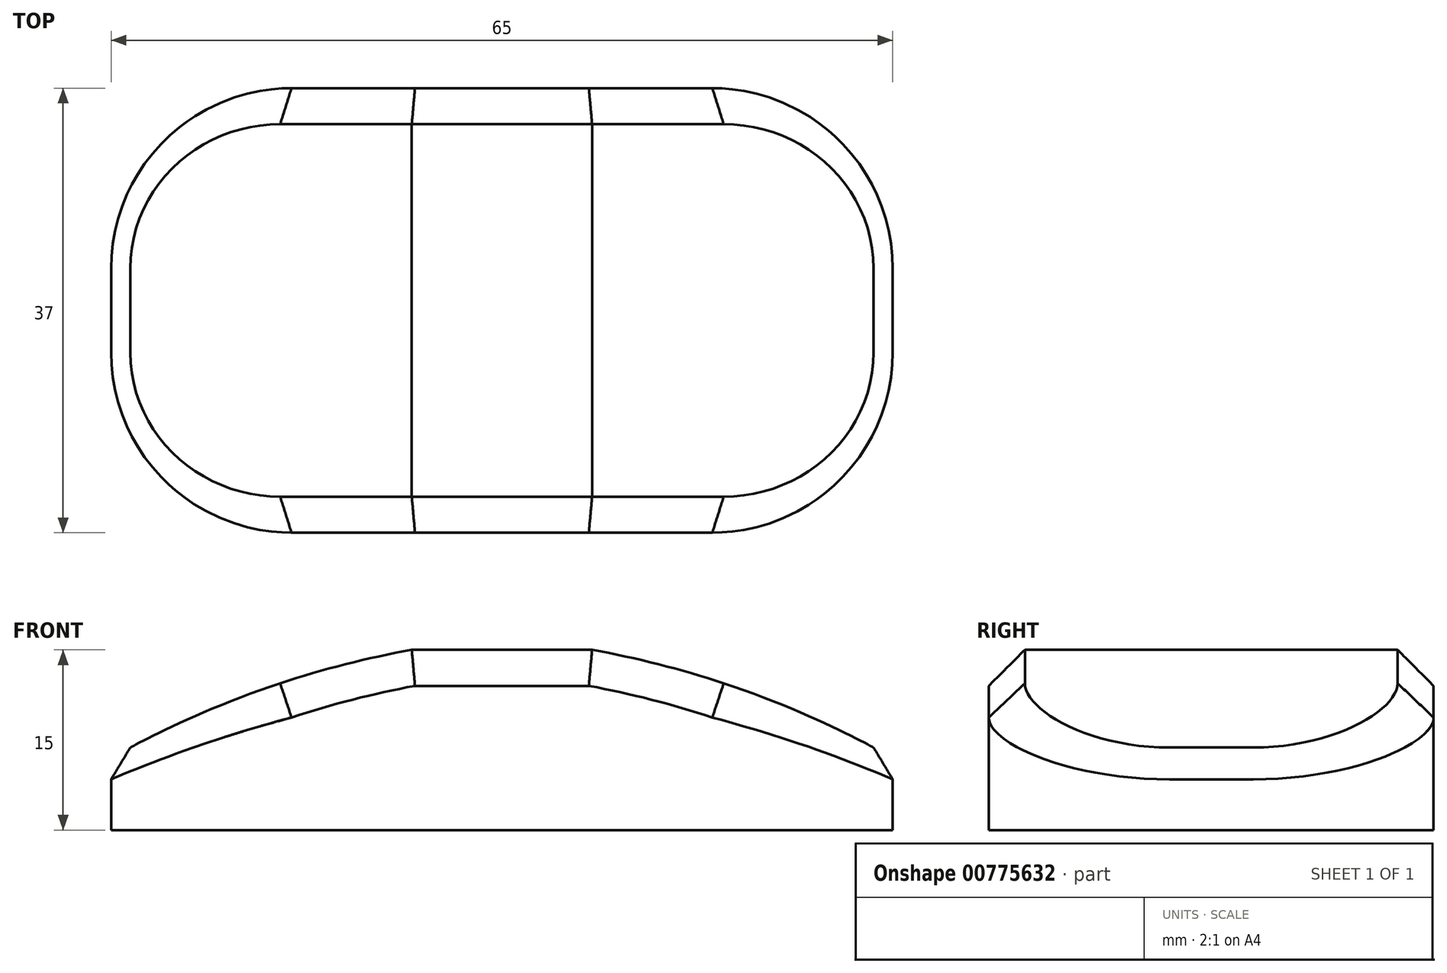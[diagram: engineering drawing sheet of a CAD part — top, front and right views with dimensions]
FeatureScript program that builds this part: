
annotation { "Feature Type Name" : "Feature", "Feature Type Description" : "" }
export const myFeature = defineFeature(function(context is Context, id is Id, definition is map)
    precondition{}
    {
        {
            var Q0;
            Q0=qCreatedBy(makeId("Top.planeOp"),FACE);
            var sketch = newSketch(context, id + "F0", { "sketchPlane" : qUnion([Q0])});
            skLineSegment(sketch, "E0.bottom", {"start": v(32.5, -18.5) * mm, "end": v(-32.5, -18.5) * mm});
            skLineSegment(sketch, "E0.top", {"start": v(32.5, 18.5) * mm, "end": v(-32.5, 18.5) * mm});
            skLineSegment(sketch, "E0.left", {"start": v(32.5, -18.5) * mm, "end": v(32.5, 18.5) * mm});
            skLineSegment(sketch, "E0.right", {"start": v(-32.5, -18.5) * mm, "end": v(-32.5, 18.5) * mm});
            skPoint(sketch, "E0.middle", {"position": v(0, 0) * mm});
            skSolve(sketch);
        }
        {
            var Q0;
            Q0=makeQuery(id+"F0.imprint","IMPRINT",FACE,{"disambiguationData":[TD([[makeQuery(id+"F0.imprint","IMPRINT",EDGE,{"derivedFrom":sQuery(id+"F0.wireOp",EDGE,"E0.bottom")}),-1.0]])]});
            extrude(context, id + "F1", {"entities" : qUnion([Q0]), "depth" : 15 * mm, "offsetDistance" : 25 * mm});
        }
        {
            var Q0;
            Q0=makeQuery(id+"F1.opExtrude","SWEPT_FACE",FACE,{"disambiguationData":[OSD([sQuery(id+"F0.wireOp",EDGE,"E0.bottom")])]});
            var sketch = newSketch(context, id + "F2", { "sketchPlane" : qUnion([Q0])});
            skLineSegment(sketch, "E1.bottom", {"start": v(-32.5, 15) * mm, "end": v(32.5, 15) * mm});
            skLineSegment(sketch, "E1.left", {"start": v(-32.5, 15) * mm, "end": v(-32.5, 6) * mm});
            skLineSegment(sketch, "E1.right", {"start": v(32.5, 15) * mm, "end": v(32.5, 0) * mm});
            skArc(sketch, "E2", {"start": v(-7.5, 15) * mm, "mid": v(-20.38, 11.55) * mm, "end": v(-32.5, 6) * mm});
            skArc(sketch, "E3", {"start": v(32.5, 6) * mm, "mid": v(20.38, 11.55) * mm, "end": v(7.5, 15) * mm});
            skSolve(sketch);
        }
        {
            var Q0;
            {var subQ0=sQuery(id+"F2.wireOp",EDGE,"E1.left");Q0=makeQuery(id+"F2.imprint","IMPRINT",FACE,{"disambiguationData":[TD([[makeQuery(id+"F2.imprint","IMPRINT",EDGE,{"derivedFrom":subQ0}),1.0]])]});}
            var Q1;
            {var subQ3=sQuery(id+"F2.wireOp",EDGE,"E3");Q1=makeQuery(id+"F2.imprint","IMPRINT",FACE,{"disambiguationData":[TD([[makeQuery(id+"F2.imprint","IMPRINT",EDGE,{"derivedFrom":subQ3}),-1.0]])]});}
            extrude(context, id + "F3", {"entities" : qUnion([Q0, Q1]), "operationType" : NewBodyOperationType.REMOVE, "endBound" : BoundingType.THROUGH_ALL, "oppositeDirection" : true, "depth" : 25 * mm, "offsetDistance" : 25 * mm});
        }
        {
            var Q0;
            Q0=makeQuery(id+"F1.opExtrude","SWEPT_EDGE",EDGE,{"disambiguationData":[OSD([sQuery(id+"F0.wireOp",EDGE,"E0.bottom"),sQuery(id+"F0.wireOp",EDGE,"E0.right")])]});
            var Q1;
            Q1=makeQuery(id+"F1.opExtrude","SWEPT_EDGE",EDGE,{"disambiguationData":[OSD([sQuery(id+"F0.wireOp",EDGE,"E0.bottom"),sQuery(id+"F0.wireOp",EDGE,"E0.left")])]});
            var Q2;
            Q2=makeQuery(id+"F1.opExtrude","SWEPT_EDGE",EDGE,{"disambiguationData":[OSD([sQuery(id+"F0.wireOp",EDGE,"E0.top"),sQuery(id+"F0.wireOp",EDGE,"E0.left")])]});
            var Q3;
            Q3=makeQuery(id+"F1.opExtrude","SWEPT_EDGE",EDGE,{"disambiguationData":[OSD([sQuery(id+"F0.wireOp",EDGE,"E0.top"),sQuery(id+"F0.wireOp",EDGE,"E0.right")])]});
            fillet(context, id + "F4", {"entities" : qUnion([Q0, Q1, Q2, Q3]), "radius" : 15 * mm, "tangentPropagation" : true, "allowEdgeOverflow" : false});
        }
        {
            var Q0;
            Q0=makeQuery(id+"F3.boolean.opBoolean","INTERSECT",EDGE,{"derivedFrom":[makeQuery(id+"F1.opExtrude","SWEPT_FACE",FACE,{"disambiguationData":[OSD([sQuery(id+"F0.wireOp",EDGE,"E0.top")])]}),makeQuery(id+"F3.opExtrude","SWEPT_FACE",FACE,{"disambiguationData":[OSD([sQuery(id+"F2.wireOp",EDGE,"E2")])]})]});
            var Q1;
            Q1=makeQuery(id+"F4.opFillet","BLEND_EDGE",EDGE,{"blendedFrom":[makeQuery(id+"F1.opExtrude","SWEPT_EDGE",EDGE,{"disambiguationData":[OSD([sQuery(id+"F0.wireOp",EDGE,"E0.top"),sQuery(id+"F0.wireOp",EDGE,"E0.right")])]}),makeQuery(id+"F3.boolean.opBoolean","COPY",FACE,{"derivedFrom":makeQuery(id+"F3.opExtrude","SWEPT_FACE",FACE,{"disambiguationData":[OSD([sQuery(id+"F2.wireOp",EDGE,"E2")])]})})],"blendedInto":[makeQuery(id+"F3.boolean.opBoolean","COPY",FACE,{"derivedFrom":makeQuery(id+"F3.opExtrude","SWEPT_FACE",FACE,{"disambiguationData":[OSD([sQuery(id+"F2.wireOp",EDGE,"E2")])]})})]});
            var Q2;
            Q2=makeQuery(id+"F4.opFillet","BLEND_EDGE",EDGE,{"blendedFrom":[makeQuery(id+"F1.opExtrude","SWEPT_EDGE",EDGE,{"disambiguationData":[OSD([sQuery(id+"F0.wireOp",EDGE,"E0.bottom"),sQuery(id+"F0.wireOp",EDGE,"E0.right")])]}),makeQuery(id+"F3.boolean.opBoolean","COPY",FACE,{"derivedFrom":makeQuery(id+"F3.opExtrude","SWEPT_FACE",FACE,{"disambiguationData":[OSD([sQuery(id+"F2.wireOp",EDGE,"E2")])]})})],"blendedInto":[makeQuery(id+"F3.boolean.opBoolean","COPY",FACE,{"derivedFrom":makeQuery(id+"F3.opExtrude","SWEPT_FACE",FACE,{"disambiguationData":[OSD([sQuery(id+"F2.wireOp",EDGE,"E2")])]})})]});
            var Q3;
            Q3=makeQuery(id+"F3.boolean.opBoolean","COPY",EDGE,{"derivedFrom":makeQuery(id+"F3.opExtrude","CAP_EDGE",EDGE,{"disambiguationData":[OSD([sQuery(id+"F2.wireOp",EDGE,"E2")])],"isStart":true})});
            var Q4;
            Q4=makeQuery(id+"F3.boolean.opBoolean","COPY",EDGE,{"derivedFrom":makeQuery(id+"F3.opExtrude","CAP_EDGE",EDGE,{"disambiguationData":[OSD([sQuery(id+"F2.wireOp",EDGE,"E3")])],"isStart":true})});
            var Q5;
            Q5=makeQuery(id+"F4.opFillet","BLEND_EDGE",EDGE,{"blendedFrom":[makeQuery(id+"F1.opExtrude","SWEPT_EDGE",EDGE,{"disambiguationData":[OSD([sQuery(id+"F0.wireOp",EDGE,"E0.bottom"),sQuery(id+"F0.wireOp",EDGE,"E0.left")])]}),makeQuery(id+"F3.boolean.opBoolean","COPY",FACE,{"derivedFrom":makeQuery(id+"F3.opExtrude","SWEPT_FACE",FACE,{"disambiguationData":[OSD([sQuery(id+"F2.wireOp",EDGE,"E3")])]})})],"blendedInto":[makeQuery(id+"F3.boolean.opBoolean","COPY",FACE,{"derivedFrom":makeQuery(id+"F3.opExtrude","SWEPT_FACE",FACE,{"disambiguationData":[OSD([sQuery(id+"F2.wireOp",EDGE,"E3")])]})})]});
            var Q6;
            Q6=makeQuery(id+"F4.opFillet","BLEND_EDGE",EDGE,{"blendedFrom":[makeQuery(id+"F1.opExtrude","SWEPT_EDGE",EDGE,{"disambiguationData":[OSD([sQuery(id+"F0.wireOp",EDGE,"E0.top"),sQuery(id+"F0.wireOp",EDGE,"E0.left")])]}),makeQuery(id+"F3.boolean.opBoolean","COPY",FACE,{"derivedFrom":makeQuery(id+"F3.opExtrude","SWEPT_FACE",FACE,{"disambiguationData":[OSD([sQuery(id+"F2.wireOp",EDGE,"E3")])]})})],"blendedInto":[makeQuery(id+"F3.boolean.opBoolean","COPY",FACE,{"derivedFrom":makeQuery(id+"F3.opExtrude","SWEPT_FACE",FACE,{"disambiguationData":[OSD([sQuery(id+"F2.wireOp",EDGE,"E3")])]})})]});
            var Q7;
            Q7=makeQuery(id+"F3.boolean.opBoolean","INTERSECT",EDGE,{"derivedFrom":[makeQuery(id+"F1.opExtrude","SWEPT_FACE",FACE,{"disambiguationData":[OSD([sQuery(id+"F0.wireOp",EDGE,"E0.top")])]}),makeQuery(id+"F3.opExtrude","SWEPT_FACE",FACE,{"disambiguationData":[OSD([sQuery(id+"F2.wireOp",EDGE,"E3")])]})]});
            var Q8;
            Q8=makeQuery(id+"F1.opExtrude","CAP_EDGE",EDGE,{"disambiguationData":[OSD([sQuery(id+"F0.wireOp",EDGE,"E0.bottom")])],"isStart":false});
            var Q9;
            Q9=makeQuery(id+"F3.boolean.opBoolean","COPY",EDGE,{"derivedFrom":makeQuery(id+"F3.opExtrude","SWEPT_EDGE",EDGE,{"disambiguationData":[OSD([sQuery(id+"F0.wireOp",EDGE,"E0.bottom"),sQuery(id+"F0.wireOp",EDGE,"E0.right"),sQuery(id+"F2.wireOp",EDGE,"E1.left"),sQuery(id+"F2.wireOp",EDGE,"E2")])]})});
            var Q10;
            Q10=makeQuery(id+"F3.boolean.opBoolean","COPY",EDGE,{"derivedFrom":makeQuery(id+"F3.opExtrude","SWEPT_EDGE",EDGE,{"disambiguationData":[OSD([sQuery(id+"F2.wireOp",EDGE,"E1.right"),sQuery(id+"F2.wireOp",EDGE,"E3")])]})});
            var Q11;
            Q11=makeQuery(id+"F1.opExtrude","CAP_EDGE",EDGE,{"disambiguationData":[OSD([sQuery(id+"F0.wireOp",EDGE,"E0.top")])],"isStart":false});
            chamfer(context, id + "F5", {"entities" : qUnion([Q0, Q1, Q2, Q3, Q4, Q5, Q6, Q7, Q8, Q9, Q10, Q11]), "width" : 3 * mm, "tangentPropagation" : true});
        }
    });
